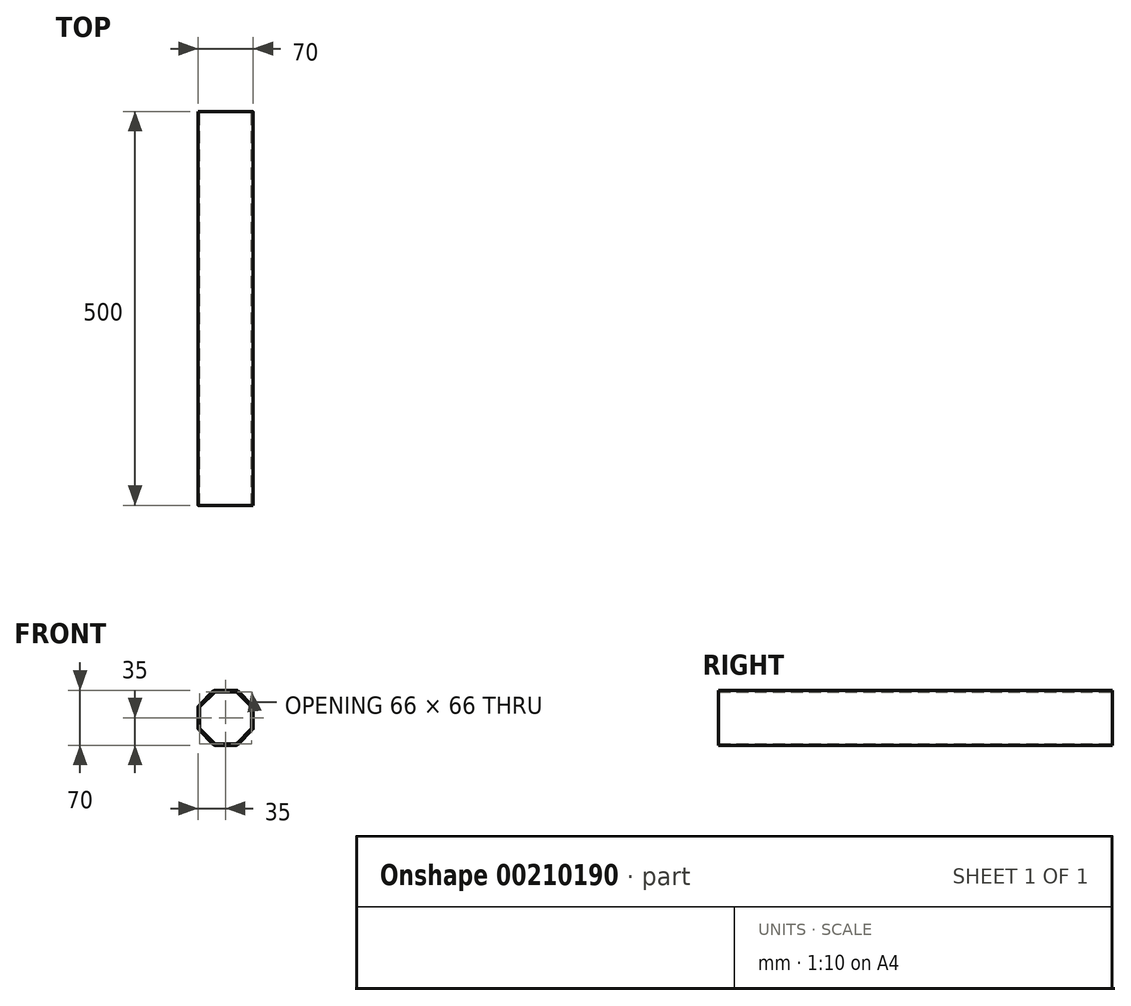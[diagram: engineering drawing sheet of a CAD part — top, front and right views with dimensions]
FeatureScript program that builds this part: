
annotation { "Feature Type Name" : "Feature", "Feature Type Description" : "" }
export const myFeature = defineFeature(function(context is Context, id is Id, definition is map)
    precondition{}
    {
        {
            var Q0;
            Q0=qCreatedBy(makeId("Front.planeOp"),FACE);
            var sketch = newSketch(context, id + "F0", { "sketchPlane" : qUnion([Q0])});
            skCircle(sketch, "E0.cCircle", {"center": v(0, 0) * mm, "radius": 35 * mm, "construction": true});
            skLineSegment(sketch, "E0.0", {"start": v(-14.5, 35) * mm, "end": v(14.5, 35) * mm});
            skLineSegment(sketch, "E0.1", {"start": v(14.5, 35) * mm, "end": v(35, 14.5) * mm});
            skLineSegment(sketch, "E0.2", {"start": v(35, 14.5) * mm, "end": v(35, -14.5) * mm});
            skLineSegment(sketch, "E0.3", {"start": v(35, -14.5) * mm, "end": v(14.5, -35) * mm});
            skLineSegment(sketch, "E0.4", {"start": v(14.5, -35) * mm, "end": v(-14.5, -35) * mm});
            skLineSegment(sketch, "E0.5", {"start": v(-14.5, -35) * mm, "end": v(-35, -14.5) * mm});
            skLineSegment(sketch, "E0.6", {"start": v(-35, -14.5) * mm, "end": v(-35, 14.5) * mm});
            skLineSegment(sketch, "E0.7", {"start": v(-35, 14.5) * mm, "end": v(-14.5, 35) * mm});
            skPoint(sketch, "E0.0.midPoint", {"position": v(0, 35) * mm});
            skLineSegment(sketch, "E1.0", {"start": v(-33, -13.67) * mm, "end": v(-33, 13.67) * mm});
            skLineSegment(sketch, "E1.1", {"start": v(-13.67, -33) * mm, "end": v(-33, -13.67) * mm});
            skLineSegment(sketch, "E1.2", {"start": v(-33, 13.67) * mm, "end": v(-13.67, 33) * mm});
            skLineSegment(sketch, "E1.3", {"start": v(13.67, -33) * mm, "end": v(-13.67, -33) * mm});
            skLineSegment(sketch, "E1.4", {"start": v(-13.67, 33) * mm, "end": v(13.67, 33) * mm});
            skLineSegment(sketch, "E1.5", {"start": v(13.67, 33) * mm, "end": v(33, 13.67) * mm});
            skLineSegment(sketch, "E1.6", {"start": v(33, 13.67) * mm, "end": v(33, -13.67) * mm});
            skLineSegment(sketch, "E1.7", {"start": v(33, -13.67) * mm, "end": v(13.67, -33) * mm});
            skSolve(sketch);
        }
        {
            var Q0;
            Q0=makeQuery(id+"F0.imprint","IMPRINT",FACE,{"disambiguationData":[TD([[makeQuery(id+"F0.imprint","IMPRINT",EDGE,{"derivedFrom":sQuery(id+"F0.wireOp",EDGE,"E0.0")}),-1.0]])]});
            extrude(context, id + "F1", {"entities" : qUnion([Q0]), "depth" : 500 * mm});
        }
        {
            var Q0;
            Q0=makeQuery(id+"F1.opExtrude","SWEPT_EDGE",EDGE,{"disambiguationData":[OSD([sQuery(id+"F0.wireOp",EDGE,"E0.0"),sQuery(id+"F0.wireOp",EDGE,"E0.1")])]});
            var Q1;
            Q1=makeQuery(id+"F1.opExtrude","SWEPT_EDGE",EDGE,{"disambiguationData":[OSD([sQuery(id+"F0.wireOp",EDGE,"E0.0"),sQuery(id+"F0.wireOp",EDGE,"E0.7")])]});
            var Q2;
            Q2=makeQuery(id+"F1.opExtrude","SWEPT_EDGE",EDGE,{"disambiguationData":[OSD([sQuery(id+"F0.wireOp",EDGE,"E0.1"),sQuery(id+"F0.wireOp",EDGE,"E0.2")])]});
            var Q3;
            Q3=makeQuery(id+"F1.opExtrude","SWEPT_EDGE",EDGE,{"disambiguationData":[OSD([sQuery(id+"F0.wireOp",EDGE,"E0.2"),sQuery(id+"F0.wireOp",EDGE,"E0.3")])]});
            var Q4;
            Q4=makeQuery(id+"F1.opExtrude","SWEPT_EDGE",EDGE,{"disambiguationData":[OSD([sQuery(id+"F0.wireOp",EDGE,"E0.3"),sQuery(id+"F0.wireOp",EDGE,"E0.4")])]});
            var Q5;
            Q5=makeQuery(id+"F1.opExtrude","SWEPT_EDGE",EDGE,{"disambiguationData":[OSD([sQuery(id+"F0.wireOp",EDGE,"E0.4"),sQuery(id+"F0.wireOp",EDGE,"E0.5")])]});
            var Q6;
            Q6=makeQuery(id+"F1.opExtrude","SWEPT_EDGE",EDGE,{"disambiguationData":[OSD([sQuery(id+"F0.wireOp",EDGE,"E0.5"),sQuery(id+"F0.wireOp",EDGE,"E0.6")])]});
            var Q7;
            Q7=makeQuery(id+"F1.opExtrude","SWEPT_EDGE",EDGE,{"disambiguationData":[OSD([sQuery(id+"F0.wireOp",EDGE,"E0.6"),sQuery(id+"F0.wireOp",EDGE,"E0.7")])]});
            fillet(context, id + "F2", {"entities" : qUnion([Q0, Q1, Q2, Q3, Q4, Q5, Q6, Q7]), "radius" : 4 * mm, "tangentPropagation" : true, "allowEdgeOverflow" : false});
        }
        {
            var Q0;
            Q0=makeQuery(id+"F1.opExtrude","SWEPT_EDGE",EDGE,{"disambiguationData":[OSD([sQuery(id+"F0.wireOp",EDGE,"E1.5"),sQuery(id+"F0.wireOp",EDGE,"E1.6")])]});
            var Q1;
            Q1=makeQuery(id+"F1.opExtrude","SWEPT_EDGE",EDGE,{"disambiguationData":[OSD([sQuery(id+"F0.wireOp",EDGE,"E1.6"),sQuery(id+"F0.wireOp",EDGE,"E1.7")])]});
            var Q2;
            Q2=makeQuery(id+"F1.opExtrude","SWEPT_EDGE",EDGE,{"disambiguationData":[OSD([sQuery(id+"F0.wireOp",EDGE,"E1.3"),sQuery(id+"F0.wireOp",EDGE,"E1.7")])]});
            var Q3;
            Q3=makeQuery(id+"F1.opExtrude","SWEPT_EDGE",EDGE,{"disambiguationData":[OSD([sQuery(id+"F0.wireOp",EDGE,"E1.1"),sQuery(id+"F0.wireOp",EDGE,"E1.3")])]});
            var Q4;
            Q4=makeQuery(id+"F1.opExtrude","SWEPT_EDGE",EDGE,{"disambiguationData":[OSD([sQuery(id+"F0.wireOp",EDGE,"E1.0"),sQuery(id+"F0.wireOp",EDGE,"E1.1")])]});
            var Q5;
            Q5=makeQuery(id+"F1.opExtrude","SWEPT_EDGE",EDGE,{"disambiguationData":[OSD([sQuery(id+"F0.wireOp",EDGE,"E1.0"),sQuery(id+"F0.wireOp",EDGE,"E1.2")])]});
            var Q6;
            Q6=makeQuery(id+"F1.opExtrude","SWEPT_EDGE",EDGE,{"disambiguationData":[OSD([sQuery(id+"F0.wireOp",EDGE,"E1.2"),sQuery(id+"F0.wireOp",EDGE,"E1.4")])]});
            var Q7;
            Q7=makeQuery(id+"F1.opExtrude","SWEPT_EDGE",EDGE,{"disambiguationData":[OSD([sQuery(id+"F0.wireOp",EDGE,"E1.4"),sQuery(id+"F0.wireOp",EDGE,"E1.5")])]});
            fillet(context, id + "F3", {"entities" : qUnion([Q0, Q1, Q2, Q3, Q4, Q5, Q6, Q7]), "radius" : 2 * mm, "tangentPropagation" : true, "allowEdgeOverflow" : false});
        }
    });
